# Revit family: WAGD - Console Outlet [Parametric]
name_source: partatom
category: Generic Models
revit_build: Autodesk Revit 2018 (Build: 20180423_1000(x64)
units: mm (PartAtom-declared; Revit-internal decimal feet)

## family parameters
Always vertical = No
Can host rebar = No
Cut with Voids When Loaded = No
Part Type = Normal
Room Calculation Point = No
Round Connector Dimension = Use Diameter
Shared = No
Work Plane-Based = Yes

## types (1)
- WAGD - Console Outlet [Parametric]
    Assembly Code = D2090100
    Default Elevation = 1219.2 mm  [stored 4 ft]
    Description = Waste Anesthetic Gas Disposal (WAGD) Console Outlet
    Laminate (Thickness) = 10 mm  [stored 0.0328084 ft]
    Manufacturer = Amico Pipeline
    Model = O-PASCONL-U-WAG
    URL = http://www.amico.com

note: [stored X ft] marks values corroborated as IEEE doubles in the binary element streams (Revit-internal decimal feet)

## geometry (parser evidence)
native form markers: Sweep x8
no freeform markers — native parametric forms only
